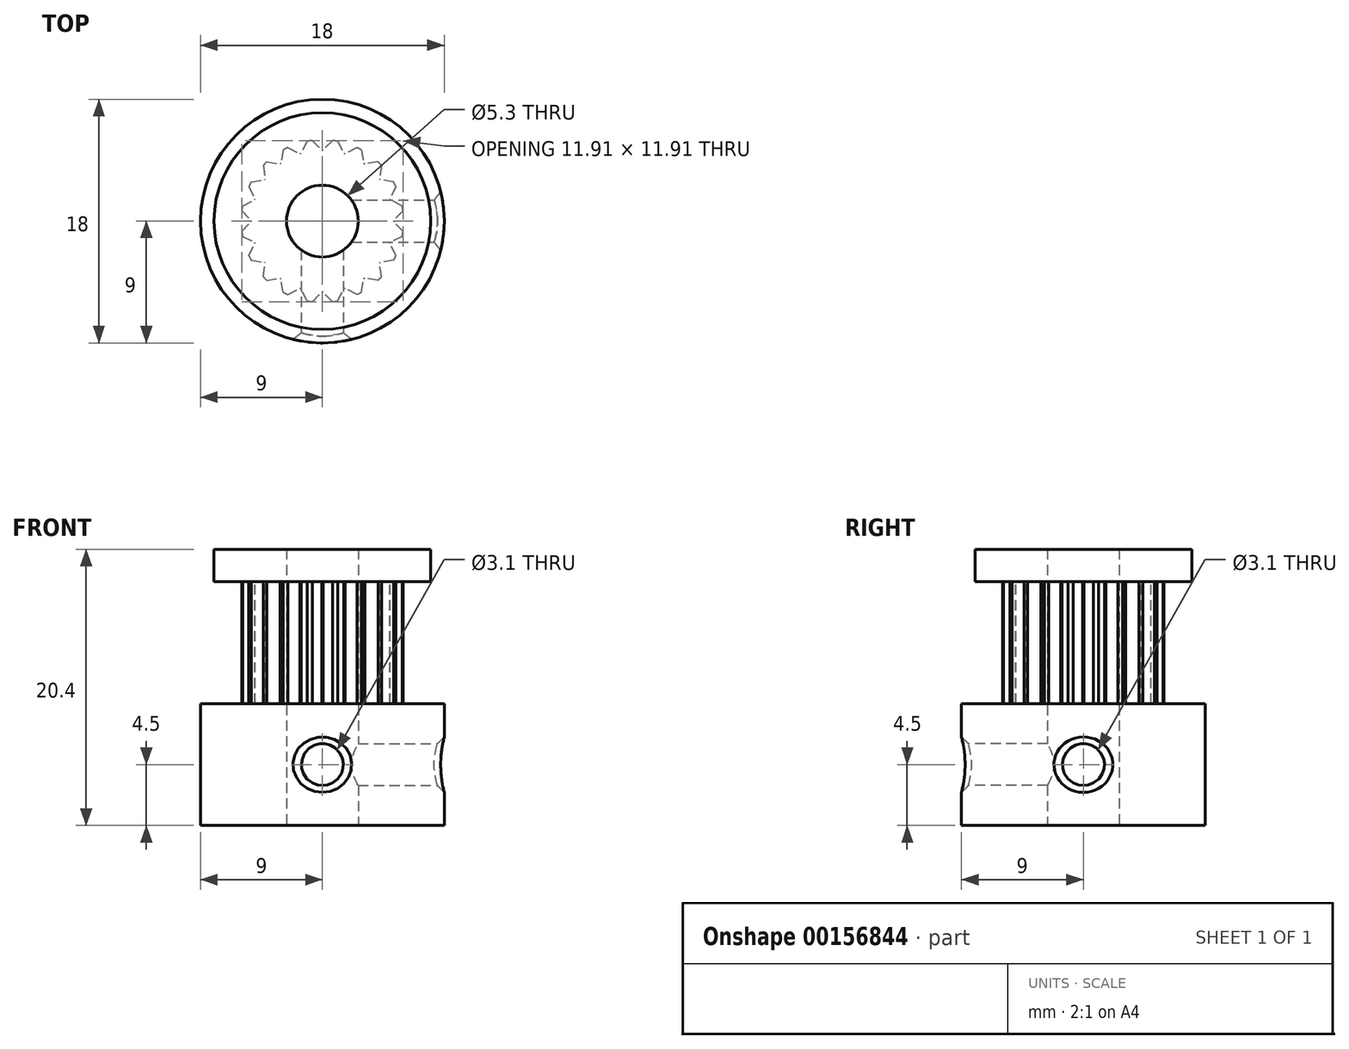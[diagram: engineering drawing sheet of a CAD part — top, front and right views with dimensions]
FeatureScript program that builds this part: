
annotation { "Feature Type Name" : "Feature", "Feature Type Description" : "" }
export const myFeature = defineFeature(function(context is Context, id is Id, definition is map)
    precondition{}
    {
        {
            var Q0;
            Q0=qCreatedBy(makeId("Top.planeOp"),FACE);
            var sketch = newSketch(context, id + "F0", { "sketchPlane" : qUnion([Q0])});
            skCircle(sketch, "E0", {"center": v(0, 0) * mm, "radius": 9 * mm});
            skCircle(sketch, "E1", {"center": v(0, 0) * mm, "radius": 2.65 * mm});
            skSolve(sketch);
        }
        {
            var Q0;
            Q0=qSketchRegion(id+"F0",true);
            extrude(context, id + "F1", {"entities" : qUnion([Q0]), "endBound" : BoundingType.SYMMETRIC, "depth" : 9 * mm});
        }
        {
            var Q0;
            Q0=qCreatedBy(makeId("Top.planeOp"),FACE);
            var sketch = newSketch(context, id + "F2", { "sketchPlane" : qUnion([Q0])});
            skLineSegment(sketch, "E2", {"start": v(1.6, 0) * mm, "end": v(9.1, 0) * mm});
            skLineSegment(sketch, "E3", {"start": v(9.1, 0) * mm, "end": v(9.1, 1.55) * mm});
            skLineSegment(sketch, "E4", {"start": v(9.1, 1.55) * mm, "end": v(1.6, 1.55) * mm});
            skLineSegment(sketch, "E5", {"start": v(1.6, 1.55) * mm, "end": v(1.6, 0) * mm});
            skSolve(sketch);
        }
        {
            var Q0;
            Q0=qSketchRegion(id+"F2",true);
            var Q1;
            Q1=sQuery(id+"F2.wireOp",EDGE,"E2");
            revolve(context, id + "F3", {"operationType" : NewBodyOperationType.REMOVE, "entities" : qUnion([Q0]), "axis" : qUnion([Q1]), "revolveType" : RevolveType.FULL, "oppositeDirection" : true});
        }
        {
            var Q0;
            Q0=qCreatedBy(makeId("Top.planeOp"),FACE);
            var sketch = newSketch(context, id + "F4", { "sketchPlane" : qUnion([Q0])});
            skLineSegment(sketch, "E6", {"start": v(0, -1.6) * mm, "end": v(0, -9.1) * mm});
            skLineSegment(sketch, "E7", {"start": v(0, -9.1) * mm, "end": v(1.55, -9.1) * mm});
            skLineSegment(sketch, "E8", {"start": v(1.55, -9.1) * mm, "end": v(1.55, -1.6) * mm});
            skLineSegment(sketch, "E9", {"start": v(1.55, -1.6) * mm, "end": v(0, -1.6) * mm});
            skSolve(sketch);
        }
        {
            var Q0;
            Q0=makeQuery(id+"F4.imprint","IMPRINT",FACE,{"disambiguationData":[TD([[makeQuery(id+"F4.imprint","IMPRINT",EDGE,{"derivedFrom":sQuery(id+"F4.wireOp",EDGE,"E6")}),1.0]])]});
            var Q1;
            Q1=sQuery(id+"F4.wireOp",EDGE,"E6");
            revolve(context, id + "F5", {"operationType" : NewBodyOperationType.REMOVE, "entities" : qUnion([Q0]), "axis" : qUnion([Q1]), "revolveType" : RevolveType.FULL, "oppositeDirection" : true});
        }
        {
            var Q0;
            Q0=makeQuery(id+"F5.boolean.opBoolean","INTERSECT",EDGE,{"derivedFrom":[makeQuery(id+"F1.opExtrude","SWEPT_FACE",FACE,{"disambiguationData":[OSD([sQuery(id+"F0.wireOp",EDGE,"E0")])]}),makeQuery(id+"F5.opRevolve","SWEPT_FACE",FACE,{"disambiguationData":[OSD([sQuery(id+"F4.wireOp",EDGE,"E8")])]})]});
            var Q1;
            Q1=makeQuery(id+"F3.boolean.opBoolean","INTERSECT",EDGE,{"derivedFrom":[makeQuery(id+"F1.opExtrude","SWEPT_FACE",FACE,{"disambiguationData":[OSD([sQuery(id+"F0.wireOp",EDGE,"E0")])]}),makeQuery(id+"F3.opRevolve","SWEPT_FACE",FACE,{"disambiguationData":[OSD([sQuery(id+"F2.wireOp",EDGE,"E4")])]})]});
            chamfer(context, id + "F6", {"entities" : qUnion([Q0, Q1]), "width" : .5 * mm, "tangentPropagation" : true});
        }
        {
            var Q0;
            Q0=makeQuery(id+"F1.opExtrude","CAP_FACE",FACE,{"disambiguationData":[OSD([sQuery(id+"F0.wireOp",EDGE,"E0"),sQuery(id+"F0.wireOp",EDGE,"E1")])],"isStart":false});
            var sketch = newSketch(context, id + "F7", { "sketchPlane" : qUnion([Q0])});
            skCircle(sketch, "E10", {"center": v(0, 0) * mm, "radius": 2.65 * mm});
            skCircle(sketch, "E11", {"center": v(0, 0) * mm, "radius": 6 * mm});
            skSolve(sketch);
        }
        {
            var Q0;
            Q0=qSketchRegion(id+"F7",true);
            extrude(context, id + "F8", {"entities" : qUnion([Q0]), "operationType" : NewBodyOperationType.ADD, "depth" : 9 * mm});
        }
        {
            var Q0;
            Q0=makeQuery(id+"F8.opExtrude","CAP_FACE",FACE,{"disambiguationData":[OSD([sQuery(id+"F7.wireOp",EDGE,"E10"),sQuery(id+"F7.wireOp",EDGE,"E11")])],"isStart":false});
            var sketch = newSketch(context, id + "F9", { "sketchPlane" : qUnion([Q0])});
            skLineSegment(sketch, "E12", {"start": v(0, 0) * mm, "end": v(6, 0) * mm, "construction": true});
            skLineSegment(sketch, "E13", {"start": v(5.95, 0.75) * mm, "end": v(5.25, 0.05) * mm});
            skLineSegment(sketch, "E14", {"start": v(5.25, 0.05) * mm, "end": v(5.25, 0) * mm});
            skArc(sketch, "E15", {"start": v(5.95, 0.75) * mm, "mid": v(5.99, 0.38) * mm, "end": v(6, 0) * mm});
            skLineSegment(sketch, "E16.MirrorCS", {"start": v(5.25, -0.05) * mm, "end": v(5.25, 0) * mm});
            skLineSegment(sketch, "E17.MirrorCS", {"start": v(5.95, -0.75) * mm, "end": v(5.25, -0.05) * mm});
            skArc(sketch, "E18.MirrorCS", {"start": v(5.95, -0.75) * mm, "mid": v(5.99, -0.38) * mm, "end": v(6, 0) * mm});
            skLineSegment(sketch, "E19.1.0", {"start": v(5.43, 2.55) * mm, "end": v(4.98, 1.67) * mm});
            skArc(sketch, "E19.1.1", {"start": v(5.43, 2.55) * mm, "mid": v(5.58, 2.2) * mm, "end": v(5.7, 1.85) * mm});
            skLineSegment(sketch, "E19.1.2", {"start": v(5.9, 1.13) * mm, "end": v(5, 1.58) * mm});
            skArc(sketch, "E19.1.3", {"start": v(5.9, 1.13) * mm, "mid": v(5.81, 1.5) * mm, "end": v(5.7, 1.85) * mm});
            skLineSegment(sketch, "E19.1.4", {"start": v(4.98, 1.67) * mm, "end": v(5, 1.62) * mm});
            skLineSegment(sketch, "E19.1.5", {"start": v(5, 1.58) * mm, "end": v(5, 1.62) * mm});
            skLineSegment(sketch, "E19.2.0", {"start": v(4.38, 4.1) * mm, "end": v(4.22, 3.12) * mm});
            skArc(sketch, "E19.2.1", {"start": v(4.38, 4.1) * mm, "mid": v(4.62, 3.82) * mm, "end": v(4.85, 3.53) * mm});
            skLineSegment(sketch, "E19.2.2", {"start": v(5.26, 2.9) * mm, "end": v(4.28, 3.05) * mm});
            skArc(sketch, "E19.2.3", {"start": v(5.26, 2.9) * mm, "mid": v(5.07, 3.22) * mm, "end": v(4.85, 3.53) * mm});
            skLineSegment(sketch, "E19.2.4", {"start": v(4.22, 3.12) * mm, "end": v(4.25, 3.09) * mm});
            skLineSegment(sketch, "E19.2.5", {"start": v(4.28, 3.05) * mm, "end": v(4.25, 3.09) * mm});
            skLineSegment(sketch, "E19.3.0", {"start": v(2.9, 5.26) * mm, "end": v(3.05, 4.28) * mm});
            skArc(sketch, "E19.3.1", {"start": v(2.9, 5.26) * mm, "mid": v(3.22, 5.07) * mm, "end": v(3.53, 4.85) * mm});
            skLineSegment(sketch, "E19.3.2", {"start": v(4.1, 4.38) * mm, "end": v(3.12, 4.22) * mm});
            skArc(sketch, "E19.3.3", {"start": v(4.1, 4.38) * mm, "mid": v(3.82, 4.62) * mm, "end": v(3.53, 4.85) * mm});
            skLineSegment(sketch, "E19.3.4", {"start": v(3.05, 4.28) * mm, "end": v(3.09, 4.25) * mm});
            skLineSegment(sketch, "E19.3.5", {"start": v(3.12, 4.22) * mm, "end": v(3.09, 4.25) * mm});
            skLineSegment(sketch, "E19.4.0", {"start": v(1.13, 5.9) * mm, "end": v(1.58, 5) * mm});
            skArc(sketch, "E19.4.1", {"start": v(1.13, 5.9) * mm, "mid": v(1.5, 5.81) * mm, "end": v(1.85, 5.7) * mm});
            skLineSegment(sketch, "E19.4.2", {"start": v(2.55, 5.43) * mm, "end": v(1.67, 4.98) * mm});
            skArc(sketch, "E19.4.3", {"start": v(2.55, 5.43) * mm, "mid": v(2.2, 5.58) * mm, "end": v(1.85, 5.7) * mm});
            skLineSegment(sketch, "E19.4.4", {"start": v(1.58, 5) * mm, "end": v(1.62, 5) * mm});
            skLineSegment(sketch, "E19.4.5", {"start": v(1.67, 4.98) * mm, "end": v(1.62, 5) * mm});
            skLineSegment(sketch, "E19.5.0", {"start": v(-0.75, 5.95) * mm, "end": v(-0.05, 5.25) * mm});
            skArc(sketch, "E19.5.1", {"start": v(-0.75, 5.95) * mm, "mid": v(-0.38, 5.99) * mm, "end": v(0, 6) * mm});
            skLineSegment(sketch, "E19.5.2", {"start": v(0.75, 5.95) * mm, "end": v(0.05, 5.25) * mm});
            skArc(sketch, "E19.5.3", {"start": v(0.75, 5.95) * mm, "mid": v(0.38, 5.99) * mm, "end": v(0, 6) * mm});
            skLineSegment(sketch, "E19.5.4", {"start": v(-0.05, 5.25) * mm, "end": v(0, 5.25) * mm});
            skLineSegment(sketch, "E19.5.5", {"start": v(0.05, 5.25) * mm, "end": v(0, 5.25) * mm});
            skLineSegment(sketch, "E19.6.0", {"start": v(-2.55, 5.43) * mm, "end": v(-1.67, 4.98) * mm});
            skArc(sketch, "E19.6.1", {"start": v(-2.55, 5.43) * mm, "mid": v(-2.2, 5.58) * mm, "end": v(-1.85, 5.7) * mm});
            skLineSegment(sketch, "E19.6.2", {"start": v(-1.13, 5.9) * mm, "end": v(-1.58, 5) * mm});
            skArc(sketch, "E19.6.3", {"start": v(-1.13, 5.9) * mm, "mid": v(-1.5, 5.81) * mm, "end": v(-1.85, 5.7) * mm});
            skLineSegment(sketch, "E19.6.4", {"start": v(-1.67, 4.98) * mm, "end": v(-1.62, 5) * mm});
            skLineSegment(sketch, "E19.6.5", {"start": v(-1.58, 5) * mm, "end": v(-1.62, 5) * mm});
            skLineSegment(sketch, "E19.7.0", {"start": v(-4.1, 4.38) * mm, "end": v(-3.12, 4.22) * mm});
            skArc(sketch, "E19.7.1", {"start": v(-4.1, 4.38) * mm, "mid": v(-3.82, 4.62) * mm, "end": v(-3.53, 4.85) * mm});
            skLineSegment(sketch, "E19.7.2", {"start": v(-2.9, 5.26) * mm, "end": v(-3.05, 4.28) * mm});
            skArc(sketch, "E19.7.3", {"start": v(-2.9, 5.26) * mm, "mid": v(-3.22, 5.07) * mm, "end": v(-3.53, 4.85) * mm});
            skLineSegment(sketch, "E19.7.4", {"start": v(-3.12, 4.22) * mm, "end": v(-3.09, 4.25) * mm});
            skLineSegment(sketch, "E19.7.5", {"start": v(-3.05, 4.28) * mm, "end": v(-3.09, 4.25) * mm});
            skLineSegment(sketch, "E19.8.0", {"start": v(-5.26, 2.9) * mm, "end": v(-4.28, 3.05) * mm});
            skArc(sketch, "E19.8.1", {"start": v(-5.26, 2.9) * mm, "mid": v(-5.07, 3.22) * mm, "end": v(-4.85, 3.53) * mm});
            skLineSegment(sketch, "E19.8.2", {"start": v(-4.38, 4.1) * mm, "end": v(-4.22, 3.12) * mm});
            skArc(sketch, "E19.8.3", {"start": v(-4.38, 4.1) * mm, "mid": v(-4.62, 3.82) * mm, "end": v(-4.85, 3.53) * mm});
            skLineSegment(sketch, "E19.8.4", {"start": v(-4.28, 3.05) * mm, "end": v(-4.25, 3.09) * mm});
            skLineSegment(sketch, "E19.8.5", {"start": v(-4.22, 3.12) * mm, "end": v(-4.25, 3.09) * mm});
            skLineSegment(sketch, "E19.9.0", {"start": v(-5.9, 1.13) * mm, "end": v(-5, 1.58) * mm});
            skArc(sketch, "E19.9.1", {"start": v(-5.9, 1.13) * mm, "mid": v(-5.81, 1.5) * mm, "end": v(-5.7, 1.85) * mm});
            skLineSegment(sketch, "E19.9.2", {"start": v(-5.43, 2.55) * mm, "end": v(-4.98, 1.67) * mm});
            skArc(sketch, "E19.9.3", {"start": v(-5.43, 2.55) * mm, "mid": v(-5.58, 2.2) * mm, "end": v(-5.7, 1.85) * mm});
            skLineSegment(sketch, "E19.9.4", {"start": v(-5, 1.58) * mm, "end": v(-5, 1.62) * mm});
            skLineSegment(sketch, "E19.9.5", {"start": v(-4.98, 1.67) * mm, "end": v(-5, 1.62) * mm});
            skLineSegment(sketch, "E19.10.0", {"start": v(-5.95, -0.75) * mm, "end": v(-5.25, -0.05) * mm});
            skArc(sketch, "E19.10.1", {"start": v(-5.95, -0.75) * mm, "mid": v(-5.99, -0.38) * mm, "end": v(-6, 0) * mm});
            skLineSegment(sketch, "E19.10.2", {"start": v(-5.95, 0.75) * mm, "end": v(-5.25, 0.05) * mm});
            skArc(sketch, "E19.10.3", {"start": v(-5.95, 0.75) * mm, "mid": v(-5.99, 0.38) * mm, "end": v(-6, 0) * mm});
            skLineSegment(sketch, "E19.10.4", {"start": v(-5.25, -0.05) * mm, "end": v(-5.25, 0) * mm});
            skLineSegment(sketch, "E19.10.5", {"start": v(-5.25, 0.05) * mm, "end": v(-5.25, 0) * mm});
            skLineSegment(sketch, "E19.11.0", {"start": v(-5.43, -2.55) * mm, "end": v(-4.98, -1.67) * mm});
            skArc(sketch, "E19.11.1", {"start": v(-5.43, -2.55) * mm, "mid": v(-5.58, -2.2) * mm, "end": v(-5.7, -1.85) * mm});
            skLineSegment(sketch, "E19.11.2", {"start": v(-5.9, -1.13) * mm, "end": v(-5, -1.58) * mm});
            skArc(sketch, "E19.11.3", {"start": v(-5.9, -1.13) * mm, "mid": v(-5.81, -1.5) * mm, "end": v(-5.7, -1.85) * mm});
            skLineSegment(sketch, "E19.11.4", {"start": v(-4.98, -1.67) * mm, "end": v(-5, -1.62) * mm});
            skLineSegment(sketch, "E19.11.5", {"start": v(-5, -1.58) * mm, "end": v(-5, -1.62) * mm});
            skLineSegment(sketch, "E19.12.0", {"start": v(-4.38, -4.1) * mm, "end": v(-4.22, -3.12) * mm});
            skArc(sketch, "E19.12.1", {"start": v(-4.38, -4.1) * mm, "mid": v(-4.62, -3.82) * mm, "end": v(-4.85, -3.53) * mm});
            skLineSegment(sketch, "E19.12.2", {"start": v(-5.26, -2.9) * mm, "end": v(-4.28, -3.05) * mm});
            skArc(sketch, "E19.12.3", {"start": v(-5.26, -2.9) * mm, "mid": v(-5.07, -3.22) * mm, "end": v(-4.85, -3.53) * mm});
            skLineSegment(sketch, "E19.12.4", {"start": v(-4.22, -3.12) * mm, "end": v(-4.25, -3.09) * mm});
            skLineSegment(sketch, "E19.12.5", {"start": v(-4.28, -3.05) * mm, "end": v(-4.25, -3.09) * mm});
            skLineSegment(sketch, "E19.13.0", {"start": v(-2.9, -5.26) * mm, "end": v(-3.05, -4.28) * mm});
            skArc(sketch, "E19.13.1", {"start": v(-2.9, -5.26) * mm, "mid": v(-3.22, -5.07) * mm, "end": v(-3.53, -4.85) * mm});
            skLineSegment(sketch, "E19.13.2", {"start": v(-4.1, -4.38) * mm, "end": v(-3.12, -4.22) * mm});
            skArc(sketch, "E19.13.3", {"start": v(-4.1, -4.38) * mm, "mid": v(-3.82, -4.62) * mm, "end": v(-3.53, -4.85) * mm});
            skLineSegment(sketch, "E19.13.4", {"start": v(-3.05, -4.28) * mm, "end": v(-3.09, -4.25) * mm});
            skLineSegment(sketch, "E19.13.5", {"start": v(-3.12, -4.22) * mm, "end": v(-3.09, -4.25) * mm});
            skLineSegment(sketch, "E19.14.0", {"start": v(-1.13, -5.9) * mm, "end": v(-1.58, -5) * mm});
            skArc(sketch, "E19.14.1", {"start": v(-1.13, -5.9) * mm, "mid": v(-1.5, -5.81) * mm, "end": v(-1.85, -5.7) * mm});
            skLineSegment(sketch, "E19.14.2", {"start": v(-2.55, -5.43) * mm, "end": v(-1.67, -4.98) * mm});
            skArc(sketch, "E19.14.3", {"start": v(-2.55, -5.43) * mm, "mid": v(-2.2, -5.58) * mm, "end": v(-1.85, -5.7) * mm});
            skLineSegment(sketch, "E19.14.4", {"start": v(-1.58, -5) * mm, "end": v(-1.62, -5) * mm});
            skLineSegment(sketch, "E19.14.5", {"start": v(-1.67, -4.98) * mm, "end": v(-1.62, -5) * mm});
            skLineSegment(sketch, "E19.15.0", {"start": v(0.75, -5.95) * mm, "end": v(0.05, -5.25) * mm});
            skArc(sketch, "E19.15.1", {"start": v(0.75, -5.95) * mm, "mid": v(0.38, -5.99) * mm, "end": v(0, -6) * mm});
            skLineSegment(sketch, "E19.15.2", {"start": v(-0.75, -5.95) * mm, "end": v(-0.05, -5.25) * mm});
            skArc(sketch, "E19.15.3", {"start": v(-0.75, -5.95) * mm, "mid": v(-0.38, -5.99) * mm, "end": v(0, -6) * mm});
            skLineSegment(sketch, "E19.15.4", {"start": v(0.05, -5.25) * mm, "end": v(0, -5.25) * mm});
            skLineSegment(sketch, "E19.15.5", {"start": v(-0.05, -5.25) * mm, "end": v(0, -5.25) * mm});
            skLineSegment(sketch, "E19.16.0", {"start": v(2.55, -5.43) * mm, "end": v(1.67, -4.98) * mm});
            skArc(sketch, "E19.16.1", {"start": v(2.55, -5.43) * mm, "mid": v(2.2, -5.58) * mm, "end": v(1.85, -5.7) * mm});
            skLineSegment(sketch, "E19.16.2", {"start": v(1.13, -5.9) * mm, "end": v(1.58, -5) * mm});
            skArc(sketch, "E19.16.3", {"start": v(1.13, -5.9) * mm, "mid": v(1.5, -5.81) * mm, "end": v(1.85, -5.7) * mm});
            skLineSegment(sketch, "E19.16.4", {"start": v(1.67, -4.98) * mm, "end": v(1.62, -5) * mm});
            skLineSegment(sketch, "E19.16.5", {"start": v(1.58, -5) * mm, "end": v(1.62, -5) * mm});
            skLineSegment(sketch, "E19.17.0", {"start": v(4.1, -4.38) * mm, "end": v(3.12, -4.22) * mm});
            skArc(sketch, "E19.17.1", {"start": v(4.1, -4.38) * mm, "mid": v(3.82, -4.62) * mm, "end": v(3.53, -4.85) * mm});
            skLineSegment(sketch, "E19.17.2", {"start": v(2.9, -5.26) * mm, "end": v(3.05, -4.28) * mm});
            skArc(sketch, "E19.17.3", {"start": v(2.9, -5.26) * mm, "mid": v(3.22, -5.07) * mm, "end": v(3.53, -4.85) * mm});
            skLineSegment(sketch, "E19.17.4", {"start": v(3.12, -4.22) * mm, "end": v(3.09, -4.25) * mm});
            skLineSegment(sketch, "E19.17.5", {"start": v(3.05, -4.28) * mm, "end": v(3.09, -4.25) * mm});
            skLineSegment(sketch, "E19.18.0", {"start": v(5.26, -2.9) * mm, "end": v(4.28, -3.05) * mm});
            skArc(sketch, "E19.18.1", {"start": v(5.26, -2.9) * mm, "mid": v(5.07, -3.22) * mm, "end": v(4.85, -3.53) * mm});
            skLineSegment(sketch, "E19.18.2", {"start": v(4.38, -4.1) * mm, "end": v(4.22, -3.12) * mm});
            skArc(sketch, "E19.18.3", {"start": v(4.38, -4.1) * mm, "mid": v(4.62, -3.82) * mm, "end": v(4.85, -3.53) * mm});
            skLineSegment(sketch, "E19.18.4", {"start": v(4.28, -3.05) * mm, "end": v(4.25, -3.09) * mm});
            skLineSegment(sketch, "E19.18.5", {"start": v(4.22, -3.12) * mm, "end": v(4.25, -3.09) * mm});
            skLineSegment(sketch, "E19.19.0", {"start": v(5.9, -1.13) * mm, "end": v(5, -1.58) * mm});
            skArc(sketch, "E19.19.1", {"start": v(5.9, -1.13) * mm, "mid": v(5.81, -1.5) * mm, "end": v(5.7, -1.85) * mm});
            skLineSegment(sketch, "E19.19.2", {"start": v(5.43, -2.55) * mm, "end": v(4.98, -1.67) * mm});
            skArc(sketch, "E19.19.3", {"start": v(5.43, -2.55) * mm, "mid": v(5.58, -2.2) * mm, "end": v(5.7, -1.85) * mm});
            skLineSegment(sketch, "E19.19.4", {"start": v(5, -1.58) * mm, "end": v(5, -1.62) * mm});
            skLineSegment(sketch, "E19.19.5", {"start": v(4.98, -1.67) * mm, "end": v(5, -1.62) * mm});
            skSolve(sketch);
        }
        {
            var Q0;
            Q0=qSketchRegion(id+"F9",true);
            extrude(context, id + "F10", {"entities" : qUnion([Q0]), "operationType" : NewBodyOperationType.REMOVE, "oppositeDirection" : true, "depth" : 9 * mm});
        }
        {
            var Q0;
            Q0=makeQuery(id+"F8.opExtrude","CAP_FACE",FACE,{"disambiguationData":[OSD([sQuery(id+"F7.wireOp",EDGE,"E10"),sQuery(id+"F7.wireOp",EDGE,"E11")])],"isStart":false});
            var sketch = newSketch(context, id + "F11", { "sketchPlane" : qUnion([Q0])});
            skCircle(sketch, "E20", {"center": v(0, 0) * mm, "radius": 2.65 * mm});
            skCircle(sketch, "E21", {"center": v(0, 0) * mm, "radius": 8 * mm});
            skSolve(sketch);
        }
        {
            var Q0;
            Q0=qSketchRegion(id+"F11",true);
            extrude(context, id + "F12", {"entities" : qUnion([Q0]), "operationType" : NewBodyOperationType.ADD, "depth" : 2.4 * mm});
        }
    });
